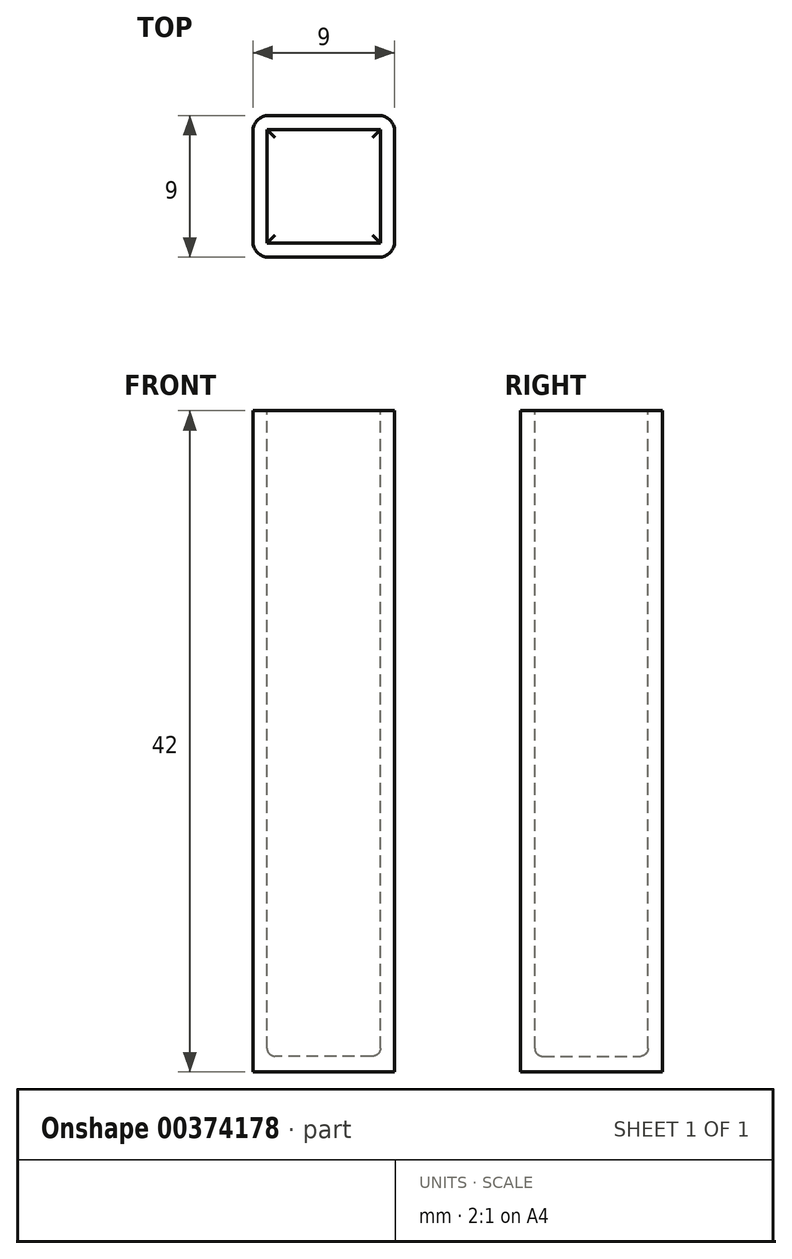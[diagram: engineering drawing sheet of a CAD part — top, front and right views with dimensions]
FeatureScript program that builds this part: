
annotation { "Feature Type Name" : "Feature", "Feature Type Description" : "" }
export const myFeature = defineFeature(function(context is Context, id is Id, definition is map)
    precondition{}
    {
        {
            var Q0;
            Q0=qCreatedBy(makeId("Top.planeOp"),FACE);
            var sketch = newSketch(context, id + "F0", { "sketchPlane" : qUnion([Q0])});
            skLineSegment(sketch, "E0.bottom", {"start": v(4.5, -4.5) * mm, "end": v(-4.5, -4.5) * mm});
            skLineSegment(sketch, "E0.top", {"start": v(4.5, 4.5) * mm, "end": v(-4.5, 4.5) * mm});
            skLineSegment(sketch, "E0.left", {"start": v(4.5, -4.5) * mm, "end": v(4.5, 4.5) * mm});
            skLineSegment(sketch, "E0.right", {"start": v(-4.5, -4.5) * mm, "end": v(-4.5, 4.5) * mm});
            skPoint(sketch, "E0.middle", {"position": v(0, 0) * mm});
            skSolve(sketch);
        }
        {
            var Q0;
            Q0=makeQuery(id+"F0.imprint","IMPRINT",FACE,{"disambiguationData":[TD([[makeQuery(id+"F0.imprint","IMPRINT",EDGE,{"derivedFrom":sQuery(id+"F0.wireOp",EDGE,"E0.bottom")}),-1.0]])]});
            extrude(context, id + "F1", {"entities" : qUnion([Q0]), "depth" : 42 * mm});
        }
        {
            var Q0;
            Q0=makeQuery(id+"F1.opExtrude","SWEPT_EDGE",EDGE,{"disambiguationData":[OSD([sQuery(id+"F0.wireOp",EDGE,"E0.bottom"),sQuery(id+"F0.wireOp",EDGE,"E0.right")])]});
            var Q1;
            Q1=makeQuery(id+"F1.opExtrude","SWEPT_EDGE",EDGE,{"disambiguationData":[OSD([sQuery(id+"F0.wireOp",EDGE,"E0.bottom"),sQuery(id+"F0.wireOp",EDGE,"E0.left")])]});
            var Q2;
            Q2=makeQuery(id+"F1.opExtrude","SWEPT_EDGE",EDGE,{"disambiguationData":[OSD([sQuery(id+"F0.wireOp",EDGE,"E0.top"),sQuery(id+"F0.wireOp",EDGE,"E0.left")])]});
            var Q3;
            Q3=makeQuery(id+"F1.opExtrude","SWEPT_EDGE",EDGE,{"disambiguationData":[OSD([sQuery(id+"F0.wireOp",EDGE,"E0.top"),sQuery(id+"F0.wireOp",EDGE,"E0.right")])]});
            fillet(context, id + "F2", {"entities" : qUnion([Q0, Q1, Q2, Q3]), "radius" : 1 * mm, "tangentPropagation" : true, "allowEdgeOverflow" : false});
        }
        {
            var Q0;
            Q0=makeQuery(id+"F1.opExtrude","CAP_FACE",FACE,{"disambiguationData":[OSD([sQuery(id+"F0.wireOp",EDGE,"E0.bottom"),sQuery(id+"F0.wireOp",EDGE,"E0.top"),sQuery(id+"F0.wireOp",EDGE,"E0.left"),sQuery(id+"F0.wireOp",EDGE,"E0.right")])],"isStart":false});
            var sketch = newSketch(context, id + "F3", { "sketchPlane" : qUnion([Q0])});
            skLineSegment(sketch, "E1.0", {"start": v(3.5, 4.5) * mm, "end": v(-3.5, 4.5) * mm});
            skArc(sketch, "E1.1", {"start": v(4.5, 3.5) * mm, "mid": v(4.2, 4.2) * mm, "end": v(3.5, 4.5) * mm});
            skArc(sketch, "E1.2", {"start": v(-3.5, 4.5) * mm, "mid": v(-4.2, 4.2) * mm, "end": v(-4.5, 3.5) * mm});
            skLineSegment(sketch, "E1.3", {"start": v(3.5, -4.5) * mm, "end": v(-3.5, -4.5) * mm});
            skLineSegment(sketch, "E1.4", {"start": v(4.5, -3.5) * mm, "end": v(4.5, 3.5) * mm});
            skLineSegment(sketch, "E1.5", {"start": v(-4.5, -3.5) * mm, "end": v(-4.5, 3.5) * mm});
            skArc(sketch, "E1.6", {"start": v(3.5, -4.5) * mm, "mid": v(4.2, -4.2) * mm, "end": v(4.5, -3.5) * mm});
            skArc(sketch, "E1.7", {"start": v(-4.5, -3.5) * mm, "mid": v(-4.2, -4.2) * mm, "end": v(-3.5, -4.5) * mm});
            skLineSegment(sketch, "E2.bottom", {"start": v(3.6, -3.6) * mm, "end": v(-3.6, -3.6) * mm});
            skLineSegment(sketch, "E2.top", {"start": v(3.6, 3.6) * mm, "end": v(-3.6, 3.6) * mm});
            skLineSegment(sketch, "E2.left", {"start": v(3.6, -3.6) * mm, "end": v(3.6, 3.6) * mm});
            skLineSegment(sketch, "E2.right", {"start": v(-3.6, -3.6) * mm, "end": v(-3.6, 3.6) * mm});
            skPoint(sketch, "E2.middle", {"position": v(0, 0) * mm});
            skSolve(sketch);
        }
        {
            var Q0;
            Q0=makeQuery(id+"F3.imprint","IMPRINT",FACE,{"disambiguationData":[TD([[makeQuery(id+"F3.imprint","IMPRINT",EDGE,{"derivedFrom":sQuery(id+"F3.wireOp",EDGE,"E2.bottom")}),-1.0]])]});
            extrude(context, id + "F4", {"entities" : qUnion([Q0]), "operationType" : NewBodyOperationType.REMOVE, "oppositeDirection" : true, "depth" : 41 * mm});
        }
        {
            var Q0;
            Q0=makeQuery(id+"F4.boolean.opBoolean","COPY",EDGE,{"derivedFrom":makeQuery(id+"F4.opExtrude","CAP_EDGE",EDGE,{"disambiguationData":[OSD([sQuery(id+"F3.wireOp",EDGE,"E2.top")])],"isStart":false})});
            var Q1;
            Q1=makeQuery(id+"F4.boolean.opBoolean","COPY",EDGE,{"derivedFrom":makeQuery(id+"F4.opExtrude","CAP_EDGE",EDGE,{"disambiguationData":[OSD([sQuery(id+"F3.wireOp",EDGE,"E2.right")])],"isStart":false})});
            var Q2;
            Q2=makeQuery(id+"F4.boolean.opBoolean","COPY",EDGE,{"derivedFrom":makeQuery(id+"F4.opExtrude","CAP_EDGE",EDGE,{"disambiguationData":[OSD([sQuery(id+"F3.wireOp",EDGE,"E2.left")])],"isStart":false})});
            var Q3;
            Q3=makeQuery(id+"F4.boolean.opBoolean","COPY",EDGE,{"derivedFrom":makeQuery(id+"F4.opExtrude","CAP_EDGE",EDGE,{"disambiguationData":[OSD([sQuery(id+"F3.wireOp",EDGE,"E2.bottom")])],"isStart":false})});
            fillet(context, id + "F5", {"entities" : qUnion([Q0, Q1, Q2, Q3]), "radius" : 0.5 * mm, "tangentPropagation" : true, "allowEdgeOverflow" : false});
        }
    });
